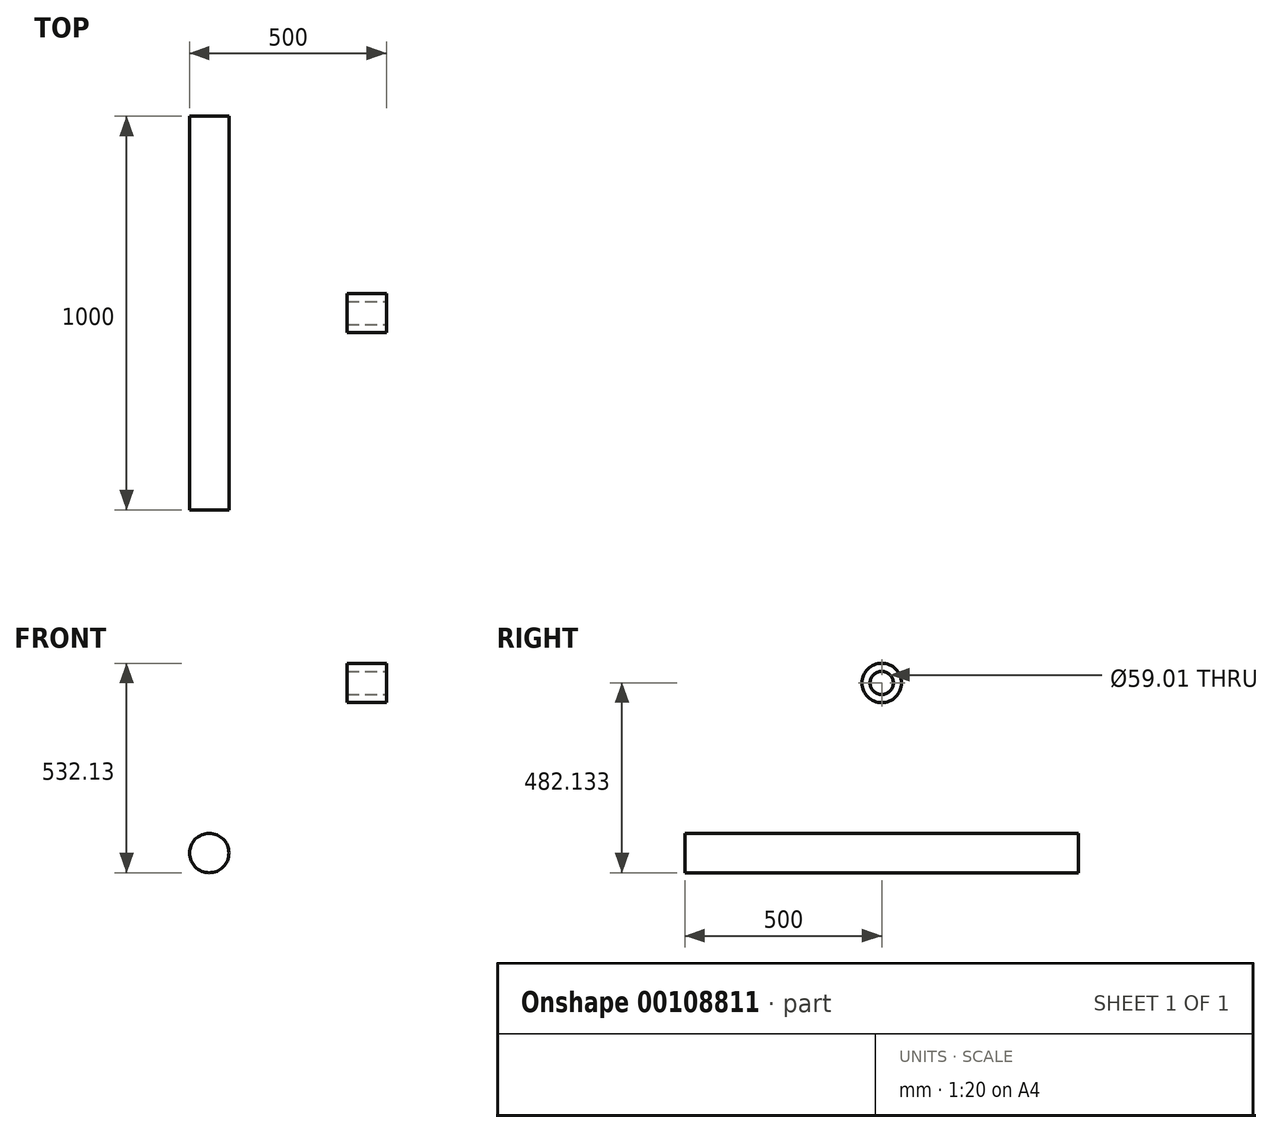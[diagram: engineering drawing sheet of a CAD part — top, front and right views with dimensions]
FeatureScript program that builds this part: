
annotation { "Feature Type Name" : "Feature", "Feature Type Description" : "" }
export const myFeature = defineFeature(function(context is Context, id is Id, definition is map)
    precondition{}
    {
        {
            var Q0;
            Q0=qCreatedBy(makeId("Front.planeOp"),FACE);
            var sketch = newSketch(context, id + "F0", { "sketchPlane" : qUnion([Q0])});
            skLineSegment(sketch, "E0", {"start": v(0, 0) * mm, "end": v(-400, 0) * mm, "construction": true});
            skCircle(sketch, "E1", {"center": v(-400, 0) * mm, "radius": 50 * mm});
            skSolve(sketch);
        }
        {
            var Q0;
            Q0 = qSketchRegion(id + "F0", true);
            extrude(context, id + "F1", {"entities" : qUnion([Q0]), "endBound" : BoundingType.SYMMETRIC, "depth" : 1000 * mm});
        }
        {
            var Q0;
            Q0=qCreatedBy(makeId("Right.planeOp"),FACE);
            var sketch = newSketch(context, id + "F2", { "sketchPlane" : qUnion([Q0])});
            skLineSegment(sketch, "E2", {"start": v(0, 0) * mm, "end": v(0, 432.13) * mm, "construction": true});
            skCircle(sketch, "E3", {"center": v(0, 432.13) * mm, "radius": 50 * mm});
            skSolve(sketch);
        }
        {
            var Q0;
            Q0 = qSketchRegion(id + "F2", true);
            extrude(context, id + "F3", {"entities" : qUnion([Q0]), "endBound" : BoundingType.SYMMETRIC, "depth" : 100 * mm});
        }
        {
            var Q0;
            Q0=makeQuery(id+"F3.opExtrude","CAP_FACE",FACE,{"disambiguationData":[OSD([sQuery(id+"F2.wireOp",EDGE,"E3")])],"isStart":false});
            var sketch = newSketch(context, id + "F4", { "sketchPlane" : qUnion([Q0])});
            skCircle(sketch, "E4", {"center": v(0, 432.13) * mm, "radius": 29.5 * mm});
            skSolve(sketch);
        }
        {
            var Q0;
            Q0 = qSketchRegion(id + "F4", true);
            extrude(context, id + "F5", {"entities" : qUnion([Q0]), "operationType" : NewBodyOperationType.REMOVE, "endBound" : BoundingType.THROUGH_ALL, "oppositeDirection" : true, "depth" : 25 * mm});
        }
        {
            var Q0;
            Q0=makeQuery(id+"F1.opExtrude","CAP_FACE",FACE,{"disambiguationData":[OSD([sQuery(id+"F0.wireOp",EDGE,"E1")])],"isStart":true});
            var sketch = newSketch(context, id + "F6", { "sketchPlane" : qUnion([Q0])});
            skLineSegment(sketch, "E5", {"start": v(400, 0) * mm, "end": v(400, 397.62) * mm, "construction": true});
            skPoint(sketch, "E6", {"position": v(400, 50) * mm});
            skSolve(sketch);
        }
        {
            var Q0;
            Q0=makeQuery(id+"F1.opExtrude","CAP_FACE",FACE,{"disambiguationData":[OSD([sQuery(id+"F0.wireOp",EDGE,"E1")])],"isStart":false});
            var sketch = newSketch(context, id + "F7", { "sketchPlane" : qUnion([Q0])});
            skPoint(sketch, "E7", {"position": v(-398.75, 49.98) * mm});
            skSolve(sketch);
        }
        {
            var Q0;
            Q0=makeQuery(id+"F3.opExtrude","CAP_FACE",FACE,{"disambiguationData":[OSD([sQuery(id+"F2.wireOp",EDGE,"E3")])],"isStart":true});
            var sketch = newSketch(context, id + "F8", { "sketchPlane" : qUnion([Q0])});
            skPoint(sketch, "E8", {"position": v(0, 482.13) * mm});
            skPoint(sketch, "E9.1.0", {"position": v(-43.3, 407.13) * mm});
            skPoint(sketch, "E9.2.0", {"position": v(43.3, 407.13) * mm});
            skPoint(sketch, "E9.center", {"position": v(0, 432.13) * mm});
            skSolve(sketch);
        }
        {
            var Q0;
            Q0=makeQuery(id+"F6.imprint","IMPRINT",FACE,{"disambiguationData":[TD([[makeQuery(id+"F6.imprint","IMPRINT",EDGE,{"derivedFrom":makeQuery(id+"F1.opExtrude","CAP_EDGE",EDGE,{"disambiguationData":[OSD([sQuery(id+"F0.wireOp",EDGE,"E1")])],"isStart":true})}),-1.0]])]});
            var sketch = newSketch(context, id + "F9", { "sketchPlane" : qUnion([Q0])});
            skLineSegment(sketch, "E10", {"start": v(402.36, 0) * mm, "end": v(305.27, 81.47) * mm, "construction": true});
            skPoint(sketch, "E11", {"position": v(362.5, 33.45) * mm});
            skSolve(sketch);
        }
        {
            var Q0;
            Q0=sQuery(id+"F7.wireOp",VERTEX,"E7");
            var Q1;
            Q1=sQuery(id+"F8.wireOp",VERTEX,"E8");
            var Q2;
            Q2=sQuery(id+"F8.wireOp",VERTEX,"E9.2.0");
            cPlane(context, id + "F10", {"entities" : qUnion([Q0, Q1, Q2]), "cplaneType" : CPlaneType.THREE_POINT, "offset" : 25 * mm, "width" : 150 * mm, "height" : 150 * mm});
        }
        {
            var Q0;
            Q0=qCreatedBy(id+"F10.planeOp",FACE);
            var sketch = newSketch(context, id + "F11", { "sketchPlane" : qUnion([Q0])});
            skFitSpline(sketch, "E12", {"points": [v(-172.63, 417.17) * mm, v(-377.35, 337.27) * mm, v(-577.85, 98.7) * mm, v(-576.6, -208.26) * mm, v(-578.27, -207.24) * mm], "startDerivative": vector(-697.64, -218.65) * mm, "endDerivative": vector(-70.51, 77.98) * mm});
            skSolve(sketch);
        }
        {
            var Q0;
            Q0=sQuery(id+"F9.wireOp",VERTEX,"E11");
            var Q1;
            Q1=sQuery(id+"F6.wireOp",VERTEX,"E6");
            var Q2;
            Q2=sQuery(id+"F7.wireOp",VERTEX,"E7");
            cPlane(context, id + "F12", {"entities" : qUnion([Q0, Q1, Q2]), "cplaneType" : CPlaneType.THREE_POINT, "offset" : 25 * mm, "width" : 150 * mm, "height" : 150 * mm});
        }
    });
